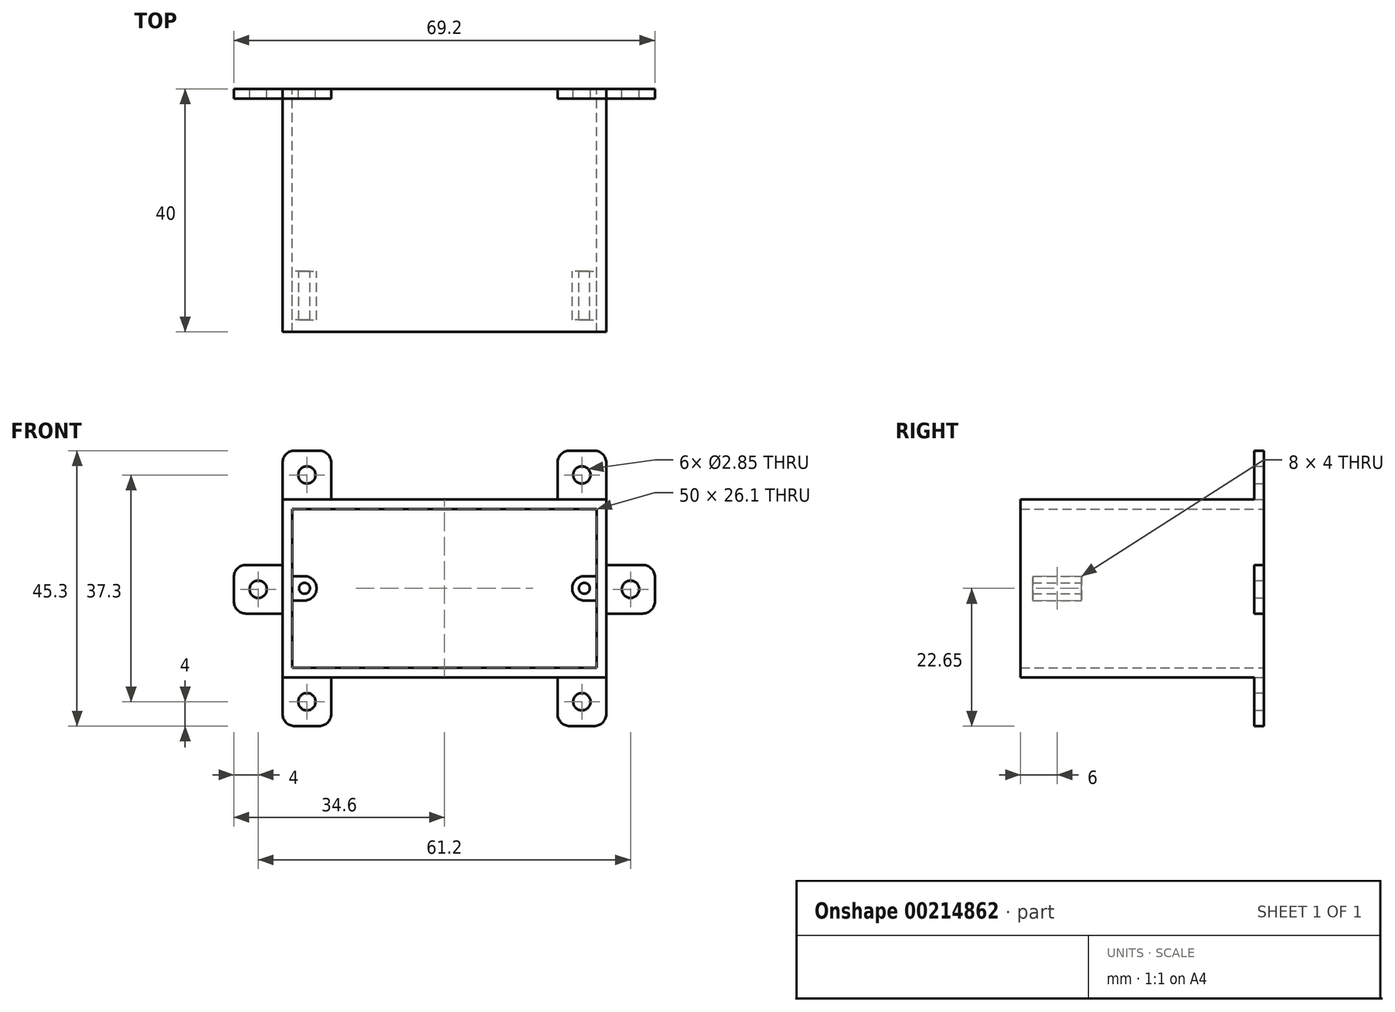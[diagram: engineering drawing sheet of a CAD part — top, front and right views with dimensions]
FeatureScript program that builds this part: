
annotation { "Feature Type Name" : "Feature", "Feature Type Description" : "" }
export const myFeature = defineFeature(function(context is Context, id is Id, definition is map)
    precondition{}
    {
        {
            var Q0;
            Q0=qCreatedBy(makeId("Front.planeOp"),FACE);
            var sketch = newSketch(context, id + "F0", { "sketchPlane" : qUnion([Q0])});
            skLineSegment(sketch, "E0.bottom", {"start": v(25, -13.05) * mm, "end": v(-25, -13.05) * mm});
            skLineSegment(sketch, "E0.top", {"start": v(25, 13.05) * mm, "end": v(-25, 13.05) * mm});
            skLineSegment(sketch, "E0.left", {"start": v(25, -13.05) * mm, "end": v(25, 13.05) * mm});
            skLineSegment(sketch, "E0.right", {"start": v(-25, -13.05) * mm, "end": v(-25, 13.05) * mm});
            skPoint(sketch, "E0.middle", {"position": v(0, 0) * mm});
            skLineSegment(sketch, "E1.0", {"start": v(-26.6, -14.65) * mm, "end": v(-26.6, 14.65) * mm});
            skLineSegment(sketch, "E1.1", {"start": v(26.6, -14.65) * mm, "end": v(-26.6, -14.65) * mm});
            skLineSegment(sketch, "E1.2", {"start": v(26.6, -14.65) * mm, "end": v(26.6, 14.65) * mm});
            skLineSegment(sketch, "E1.3", {"start": v(26.6, 14.65) * mm, "end": v(-26.6, 14.65) * mm});
            skLineSegment(sketch, "E2.bottom", {"start": v(-26.6, 14.65) * mm, "end": v(-18.6, 14.65) * mm});
            skLineSegment(sketch, "E2.top", {"start": v(-26.6, 22.65) * mm, "end": v(-18.6, 22.65) * mm});
            skLineSegment(sketch, "E2.left", {"start": v(-26.6, 14.65) * mm, "end": v(-26.6, 22.65) * mm});
            skLineSegment(sketch, "E2.right", {"start": v(-18.6, 14.65) * mm, "end": v(-18.6, 22.65) * mm});
            skLineSegment(sketch, "E3.bottom", {"start": v(34.6, -4.15) * mm, "end": v(26.6, -4.15) * mm});
            skLineSegment(sketch, "E3.top", {"start": v(34.6, 3.85) * mm, "end": v(26.6, 3.85) * mm});
            skLineSegment(sketch, "E3.left", {"start": v(34.6, -4.15) * mm, "end": v(34.6, 3.85) * mm});
            skPoint(sketch, "E3.middle", {"position": v(26.6, 0) * mm});
            skLineSegment(sketch, "E4.MirrorCS", {"start": v(-26.6, -14.65) * mm, "end": v(-26.6, -22.65) * mm});
            skLineSegment(sketch, "E5.MirrorCS", {"start": v(-26.6, -22.65) * mm, "end": v(-18.6, -22.65) * mm});
            skLineSegment(sketch, "E6.MirrorCS", {"start": v(-18.6, -14.65) * mm, "end": v(-18.6, -22.65) * mm});
            skLineSegment(sketch, "E7.MirrorCS", {"start": v(-26.6, -14.65) * mm, "end": v(-18.6, -14.65) * mm});
            skLineSegment(sketch, "E8.MirrorCS", {"start": v(18.6, 14.65) * mm, "end": v(18.6, 22.65) * mm});
            skLineSegment(sketch, "E9.MirrorCS", {"start": v(26.6, 22.65) * mm, "end": v(18.6, 22.65) * mm});
            skLineSegment(sketch, "E10.MirrorCS", {"start": v(26.6, 14.65) * mm, "end": v(26.6, 22.65) * mm});
            skLineSegment(sketch, "E11.MirrorCS", {"start": v(26.6, 14.65) * mm, "end": v(18.6, 14.65) * mm});
            skLineSegment(sketch, "E12.MirrorCS", {"start": v(26.6, -14.65) * mm, "end": v(18.6, -14.65) * mm});
            skLineSegment(sketch, "E13.MirrorCS", {"start": v(26.6, -14.65) * mm, "end": v(26.6, -22.65) * mm});
            skLineSegment(sketch, "E14.MirrorCS", {"start": v(26.6, -22.65) * mm, "end": v(18.6, -22.65) * mm});
            skLineSegment(sketch, "E15.MirrorCS", {"start": v(18.6, -14.65) * mm, "end": v(18.6, -22.65) * mm});
            skLineSegment(sketch, "E16.MirrorCS", {"start": v(-34.6, 3.85) * mm, "end": v(-26.6, 3.85) * mm});
            skLineSegment(sketch, "E17.MirrorCS", {"start": v(-34.6, -4.15) * mm, "end": v(-34.6, 3.85) * mm});
            skLineSegment(sketch, "E18.MirrorCS", {"start": v(-34.6, -4.15) * mm, "end": v(-26.6, -4.15) * mm});
            skLineSegment(sketch, "E19", {"start": v(-26.6, 22.65) * mm, "end": v(-18.6, 14.65) * mm, "construction": true});
            skLineSegment(sketch, "E20", {"start": v(-18.6, 22.65) * mm, "end": v(-26.6, 14.65) * mm, "construction": true});
            skCircle(sketch, "E21", {"center": v(-22.6, 18.65) * mm, "radius": 1.43 * mm});
            skCircle(sketch, "E22.MirrorC", {"center": v(22.6, 18.65) * mm, "radius": 1.43 * mm});
            skCircle(sketch, "E23.MirrorC", {"center": v(-22.6, -18.65) * mm, "radius": 1.43 * mm});
            skCircle(sketch, "E24.MirrorC", {"center": v(22.6, -18.65) * mm, "radius": 1.43 * mm});
            skLineSegment(sketch, "E25", {"start": v(-34.6, 3.85) * mm, "end": v(-26.6, -4.15) * mm, "construction": true});
            skLineSegment(sketch, "E26", {"start": v(-34.6, -4.15) * mm, "end": v(-26.6, 3.85) * mm, "construction": true});
            skCircle(sketch, "E27", {"center": v(-30.6, -0.15) * mm, "radius": 1.43 * mm});
            skCircle(sketch, "E28.MirrorC", {"center": v(30.6, -0.15) * mm, "radius": 1.43 * mm});
            skLineSegment(sketch, "E29.top", {"start": v(21, -2) * mm, "end": v(25, -2) * mm});
            skLineSegment(sketch, "E29.left", {"start": v(21, 2) * mm, "end": v(21, -2) * mm});
            skPoint(sketch, "E29.middle", {"position": v(25, 0) * mm});
            skLineSegment(sketch, "E30", {"start": v(21, 2) * mm, "end": v(25, 2) * mm});
            skLineSegment(sketch, "E31", {"start": v(25, 2) * mm, "end": v(21, -2) * mm, "construction": true});
            skLineSegment(sketch, "E32", {"start": v(21, 2) * mm, "end": v(25, -2) * mm, "construction": true});
            skCircle(sketch, "E33", {"center": v(23, 0) * mm, "radius": 0.9 * mm});
            skSolve(sketch);
        }
        {
            var Q0;
            Q0=makeQuery(id+"F0.imprint","IMPRINT",FACE,{"disambiguationData":[TD([[makeQuery(id+"F0.imprint","IMPRINT",EDGE,{"derivedFrom":sQuery(id+"F0.wireOp",EDGE,"E0.bottom")}),1.0]])]});
            extrude(context, id + "F1", {"entities" : qUnion([Q0]), "depth" : 40 * mm});
        }
        {
            var Q0;
            Q0 = qSketchRegion(id + "F0", true);
            extrude(context, id + "F2", {"entities" : qUnion([Q0]), "operationType" : NewBodyOperationType.ADD, "depth" : 1.6 * mm});
        }
        {
            var Q0;
            Q0=makeQuery(id+"F2.opExtrude","SWEPT_EDGE",EDGE,{"disambiguationData":[OSD([sQuery(id+"F0.wireOp",EDGE,"E2.top"),sQuery(id+"F0.wireOp",EDGE,"E2.left")])]});
            var Q1;
            Q1=makeQuery(id+"F2.opExtrude","SWEPT_EDGE",EDGE,{"disambiguationData":[OSD([sQuery(id+"F0.wireOp",EDGE,"E2.top"),sQuery(id+"F0.wireOp",EDGE,"E2.right")])]});
            var Q2;
            Q2=makeQuery(id+"F2.opExtrude","SWEPT_EDGE",EDGE,{"disambiguationData":[OSD([sQuery(id+"F0.wireOp",EDGE,"E8.MirrorCS"),sQuery(id+"F0.wireOp",EDGE,"E9.MirrorCS")])]});
            var Q3;
            Q3=makeQuery(id+"F2.opExtrude","SWEPT_EDGE",EDGE,{"disambiguationData":[OSD([sQuery(id+"F0.wireOp",EDGE,"E9.MirrorCS"),sQuery(id+"F0.wireOp",EDGE,"E10.MirrorCS")])]});
            var Q4;
            Q4=makeQuery(id+"F2.opExtrude","SWEPT_EDGE",EDGE,{"disambiguationData":[OSD([sQuery(id+"F0.wireOp",EDGE,"E3.top"),sQuery(id+"F0.wireOp",EDGE,"E3.left")])]});
            var Q5;
            Q5=makeQuery(id+"F2.opExtrude","SWEPT_EDGE",EDGE,{"disambiguationData":[OSD([sQuery(id+"F0.wireOp",EDGE,"E3.bottom"),sQuery(id+"F0.wireOp",EDGE,"E3.left")])]});
            var Q6;
            Q6=makeQuery(id+"F2.opExtrude","SWEPT_EDGE",EDGE,{"disambiguationData":[OSD([sQuery(id+"F0.wireOp",EDGE,"E13.MirrorCS"),sQuery(id+"F0.wireOp",EDGE,"E14.MirrorCS")])]});
            var Q7;
            Q7=makeQuery(id+"F2.opExtrude","SWEPT_EDGE",EDGE,{"disambiguationData":[OSD([sQuery(id+"F0.wireOp",EDGE,"E14.MirrorCS"),sQuery(id+"F0.wireOp",EDGE,"E15.MirrorCS")])]});
            var Q8;
            Q8=makeQuery(id+"F2.opExtrude","SWEPT_EDGE",EDGE,{"disambiguationData":[OSD([sQuery(id+"F0.wireOp",EDGE,"E17.MirrorCS"),sQuery(id+"F0.wireOp",EDGE,"E18.MirrorCS")])]});
            var Q9;
            Q9=makeQuery(id+"F2.opExtrude","SWEPT_EDGE",EDGE,{"disambiguationData":[OSD([sQuery(id+"F0.wireOp",EDGE,"E16.MirrorCS"),sQuery(id+"F0.wireOp",EDGE,"E17.MirrorCS")])]});
            var Q10;
            Q10=makeQuery(id+"F2.opExtrude","SWEPT_EDGE",EDGE,{"disambiguationData":[OSD([sQuery(id+"F0.wireOp",EDGE,"E4.MirrorCS"),sQuery(id+"F0.wireOp",EDGE,"E5.MirrorCS")])]});
            fillet(context, id + "F3", {"entities" : qUnion([Q0, Q1, Q2, Q3, Q4, Q5, Q6, Q7, Q8, Q9, Q10]), "radius" : 2 * mm, "tangentPropagation" : true, "allowEdgeOverflow" : false});
        }
        {
            var Q0;
            Q0=makeQuery(id+"F1.opExtrude","SWEPT_BODY",BODY,{"disambiguationData":[OSD([sQuery(id+"F0.wireOp",EDGE,"E0.bottom"),sQuery(id+"F0.wireOp",EDGE,"E0.top"),sQuery(id+"F0.wireOp",EDGE,"E0.left"),sQuery(id+"F0.wireOp",EDGE,"E0.right"),sQuery(id+"F0.wireOp",EDGE,"E1.0"),sQuery(id+"F0.wireOp",EDGE,"E1.1"),sQuery(id+"F0.wireOp",EDGE,"E1.2"),sQuery(id+"F0.wireOp",EDGE,"E1.3"),sQuery(id+"F0.wireOp",EDGE,"E2.bottom"),sQuery(id+"F0.wireOp",EDGE,"E7.MirrorCS"),sQuery(id+"F0.wireOp",EDGE,"E11.MirrorCS"),sQuery(id+"F0.wireOp",EDGE,"E12.MirrorCS")])]});
            var Q1;
            Q1=qCreatedBy(makeId("Right.planeOp"),FACE);
            mirror(context, id + "F4", {"operationType" : NewBodyOperationType.ADD, "entities" : qUnion([Q0]), "mirrorPlane" : qUnion([Q1])});
        }
        {
            var Q0;
            Q0=makeQuery(id+"F2.opExtrude","SWEPT_EDGE",EDGE,{"disambiguationData":[OSD([sQuery(id+"F0.wireOp",EDGE,"E5.MirrorCS"),sQuery(id+"F0.wireOp",EDGE,"E6.MirrorCS")])]});
            var Q1;
            Q1=makeQuery(id+"F4.opPattern","COPY",EDGE,{"derivedFrom":makeQuery(id+"F2.opExtrude","SWEPT_EDGE",EDGE,{"disambiguationData":[OSD([sQuery(id+"F0.wireOp",EDGE,"E5.MirrorCS"),sQuery(id+"F0.wireOp",EDGE,"E6.MirrorCS")])]}),"instanceName":"1"});
            fillet(context, id + "F5", {"entities" : qUnion([Q0, Q1]), "radius" : 2 * mm, "tangentPropagation" : true, "allowEdgeOverflow" : false});
        }
        {
            var Q0;
            {var subQ1=sQuery(id+"F0.wireOp",EDGE,"E29.top");Q0=makeQuery(id+"F0.imprint","IMPRINT",FACE,{"disambiguationData":[TD([[makeQuery(id+"F0.imprint","IMPRINT",EDGE,{"derivedFrom":subQ1}),1.0]])]});}
            extrude(context, id + "F6", {"entities" : qUnion([Q0]), "operationType" : NewBodyOperationType.ADD, "depth" : 38 * mm, "hasSecondDirection" : true, "secondDirectionOppositeDirection" : false, "secondDirectionDepth" : 30 * mm});
        }
        {
            var Q0;
            Q0=makeQuery(id+"F6.opExtrude","SWEPT_EDGE",EDGE,{"disambiguationData":[OSD([sQuery(id+"F0.wireOp",EDGE,"E0.left"),sQuery(id+"F0.wireOp",EDGE,"E29.top")])]});
            var Q1;
            Q1=makeQuery(id+"F6.opExtrude","SWEPT_EDGE",EDGE,{"disambiguationData":[OSD([sQuery(id+"F0.wireOp",EDGE,"E29.top"),sQuery(id+"F0.wireOp",EDGE,"E29.left")])]});
            var Q2;
            Q2=makeQuery(id+"F6.opExtrude","SWEPT_EDGE",EDGE,{"disambiguationData":[OSD([sQuery(id+"F0.wireOp",EDGE,"E29.left"),sQuery(id+"F0.wireOp",EDGE,"E30")])]});
            var Q3;
            Q3=makeQuery(id+"F6.opExtrude","SWEPT_EDGE",EDGE,{"disambiguationData":[OSD([sQuery(id+"F0.wireOp",EDGE,"E0.left"),sQuery(id+"F0.wireOp",EDGE,"E30")])]});
            var Q4;
            Q4=makeQuery(id+"F6.opExtrude","CAP_EDGE",EDGE,{"disambiguationData":[OSD([sQuery(id+"F0.wireOp",EDGE,"E0.left")])],"isStart":true});
            fillet(context, id + "F7", {"entities" : qUnion([Q0, Q1, Q2, Q3, Q4]), "radius" : 2 * mm, "tangentPropagation" : true, "allowEdgeOverflow" : false});
        }
        {
            var Q0;
            Q0=makeQuery(id+"F1.opExtrude","SWEPT_BODY",BODY,{"disambiguationData":[OSD([sQuery(id+"F0.wireOp",EDGE,"E0.bottom"),sQuery(id+"F0.wireOp",EDGE,"E0.top"),sQuery(id+"F0.wireOp",EDGE,"E0.left"),sQuery(id+"F0.wireOp",EDGE,"E0.right"),sQuery(id+"F0.wireOp",EDGE,"E1.0"),sQuery(id+"F0.wireOp",EDGE,"E1.1"),sQuery(id+"F0.wireOp",EDGE,"E1.2"),sQuery(id+"F0.wireOp",EDGE,"E1.3"),sQuery(id+"F0.wireOp",EDGE,"E2.bottom"),sQuery(id+"F0.wireOp",EDGE,"E7.MirrorCS"),sQuery(id+"F0.wireOp",EDGE,"E11.MirrorCS"),sQuery(id+"F0.wireOp",EDGE,"E12.MirrorCS")])]});
            var Q1;
            Q1=qCreatedBy(makeId("Right.planeOp"),FACE);
            mirror(context, id + "F8", {"operationType" : NewBodyOperationType.ADD, "entities" : qUnion([Q0]), "mirrorPlane" : qUnion([Q1])});
        }
    });
